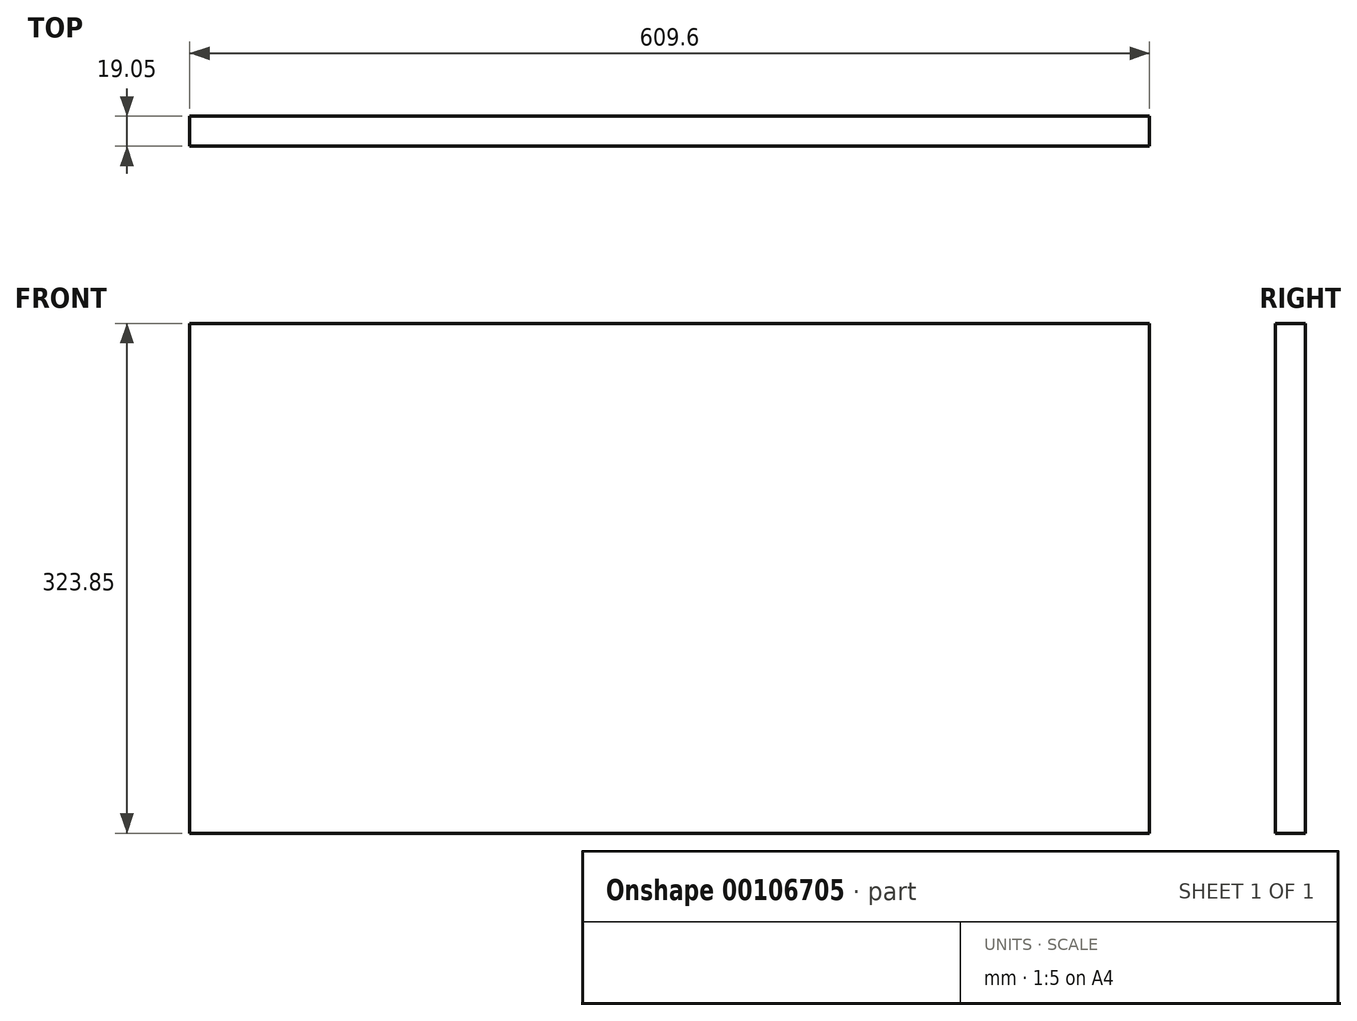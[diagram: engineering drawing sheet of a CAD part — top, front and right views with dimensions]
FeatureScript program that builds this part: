
annotation { "Feature Type Name" : "Feature", "Feature Type Description" : "" }
export const myFeature = defineFeature(function(context is Context, id is Id, definition is map)
    precondition{}
    {
        {
            var Q0;
            Q0=qCreatedBy(makeId("Front.planeOp"),FACE);
            var sketch = newSketch(context, id + "F0", { "sketchPlane" : qUnion([Q0])});
            skLineSegment(sketch, "E0.bottom", {"start": v(0, 0) * mm, "end": v(609.6, 0) * mm});
            skLineSegment(sketch, "E0.top", {"start": v(0, 323.85) * mm, "end": v(609.6, 323.85) * mm});
            skLineSegment(sketch, "E0.left", {"start": v(0, 0) * mm, "end": v(0, 323.85) * mm});
            skLineSegment(sketch, "E0.right", {"start": v(609.6, 0) * mm, "end": v(609.6, 323.85) * mm});
            skSolve(sketch);
        }
        {
            var Q0;
            Q0=makeQuery(id+"F0.imprint","IMPRINT",FACE,{"disambiguationData":[TD([[makeQuery(id+"F0.imprint","IMPRINT",EDGE,{"derivedFrom":sQuery(id+"F0.wireOp",EDGE,"E0.bottom")}),1.0]])]});
            extrude(context, id + "F1", {"entities" : qUnion([Q0]), "depth" : 19.05 * mm});
        }
    });
